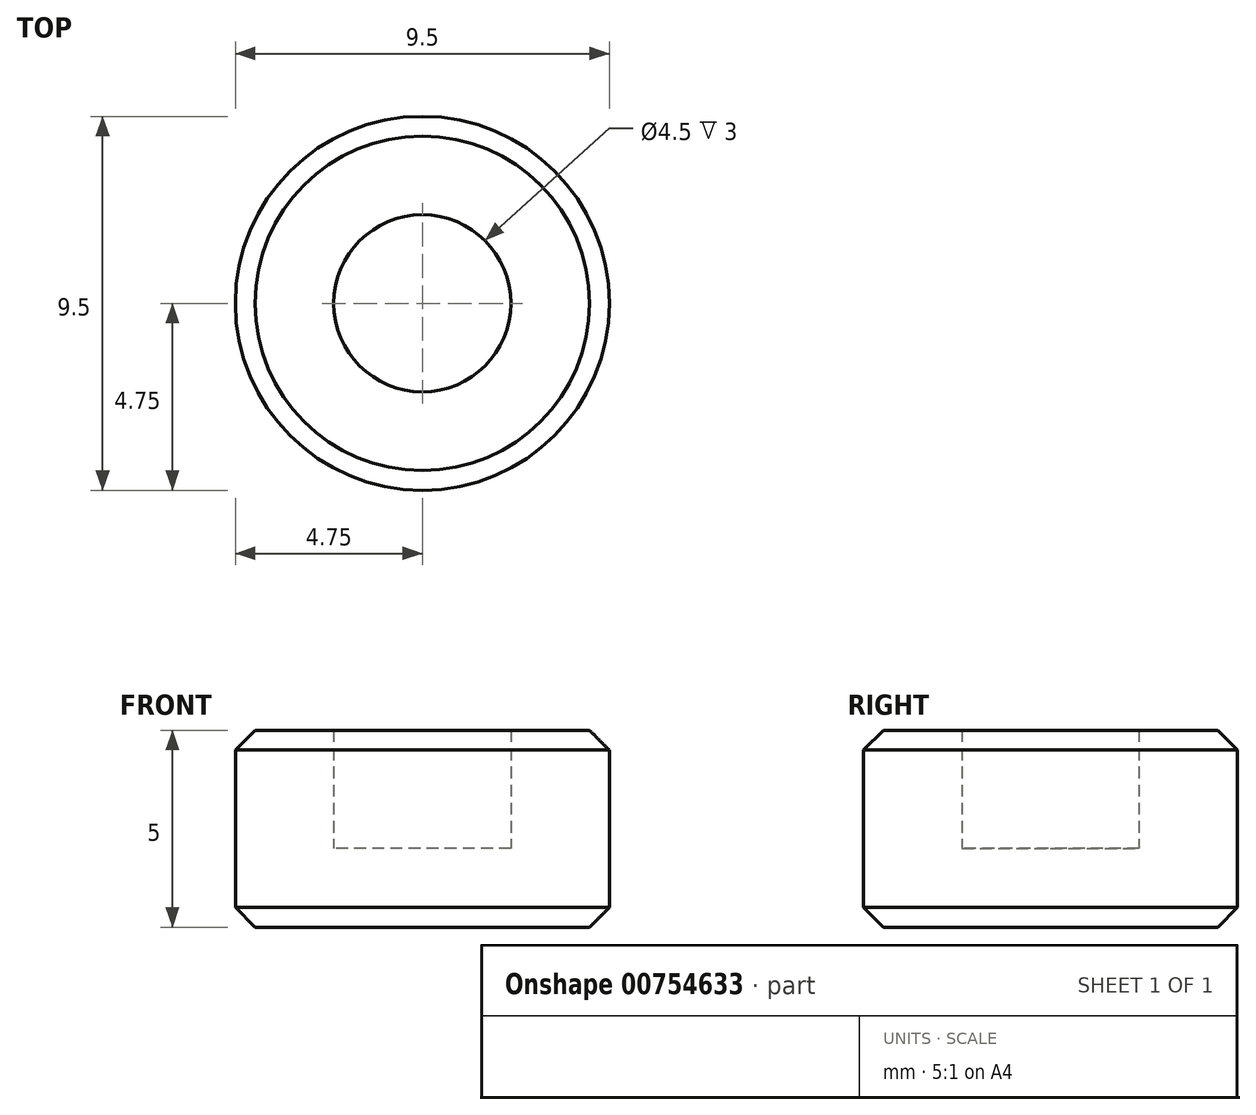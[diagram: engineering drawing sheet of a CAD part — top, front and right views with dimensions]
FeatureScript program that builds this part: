
annotation { "Feature Type Name" : "Feature", "Feature Type Description" : "" }
export const myFeature = defineFeature(function(context is Context, id is Id, definition is map)
    precondition{}
    {
        {
            var Q0;
            Q0=qCreatedBy(makeId("Top.planeOp"),FACE);
            var sketch = newSketch(context, id + "F0", { "sketchPlane" : qUnion([Q0])});
            skCircle(sketch, "E0", {"center": v(0, 0) * mm, "radius": 4.75 * mm});
            skCircle(sketch, "E1", {"center": v(0, 0) * mm, "radius": 2.25 * mm});
            skSolve(sketch);
        }
        {
            var Q0;
            Q0=makeQuery(id+"F0.imprint","IMPRINT",FACE,{"disambiguationData":[TD([[makeQuery(id+"F0.imprint","IMPRINT",EDGE,{"derivedFrom":sQuery(id+"F0.wireOp",EDGE,"E0")}),1.0]])]});
            extrude(context, id + "F1", {"entities" : qUnion([Q0]), "depth" : 3 * mm, "offsetDistance" : 25 * mm});
        }
        {
            var Q0;
            Q0=makeQuery(id+"F0.imprint","IMPRINT",FACE,{"disambiguationData":[TD([[makeQuery(id+"F0.imprint","IMPRINT",EDGE,{"derivedFrom":sQuery(id+"F0.wireOp",EDGE,"E1")}),1.0]])]});
            var Q1;
            Q1=makeQuery(id+"F0.imprint","IMPRINT",FACE,{"disambiguationData":[TD([[makeQuery(id+"F0.imprint","IMPRINT",EDGE,{"derivedFrom":sQuery(id+"F0.wireOp",EDGE,"E0")}),1.0]])]});
            extrude(context, id + "F2", {"entities" : qUnion([Q0, Q1]), "operationType" : NewBodyOperationType.ADD, "oppositeDirection" : true, "depth" : 2 * mm, "offsetDistance" : 25 * mm});
        }
        {
            var Q0;
            Q0=makeQuery(id+"F1.opExtrude","CAP_EDGE",EDGE,{"disambiguationData":[OSD([sQuery(id+"F0.wireOp",EDGE,"E0")])],"isStart":false});
            var Q1;
            Q1=makeQuery(id+"F2.opExtrude","CAP_EDGE",EDGE,{"disambiguationData":[OSD([sQuery(id+"F0.wireOp",EDGE,"E0")])],"isStart":false});
            chamfer(context, id + "F3", {"entities" : qUnion([Q0, Q1]), "width" : 0.5 * mm, "tangentPropagation" : true});
        }
    });
